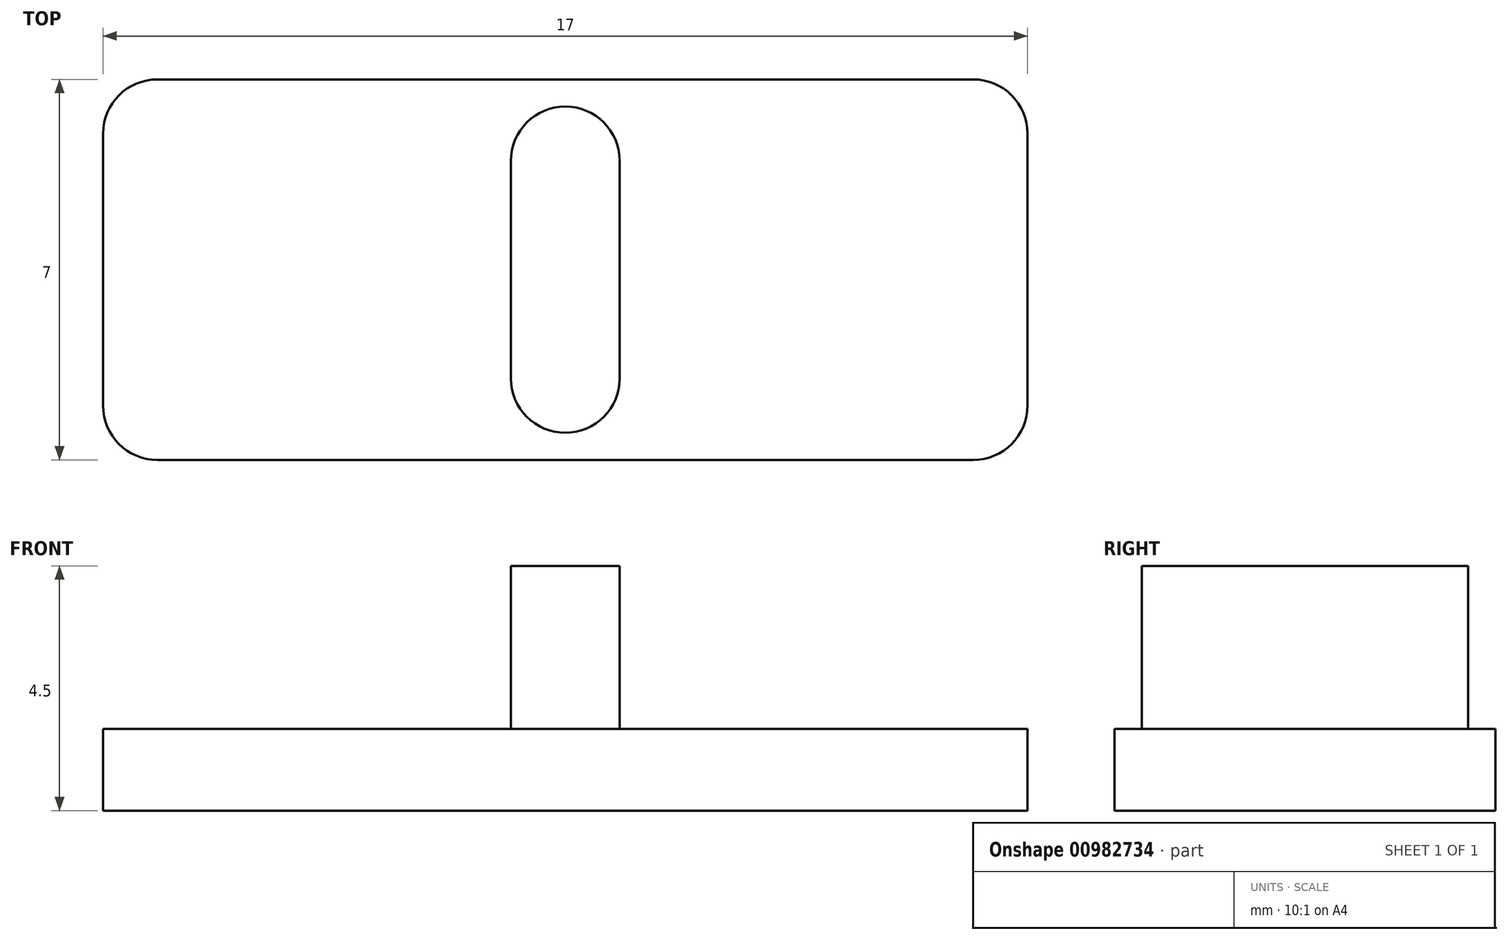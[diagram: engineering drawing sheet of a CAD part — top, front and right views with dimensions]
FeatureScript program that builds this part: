
annotation { "Feature Type Name" : "Feature", "Feature Type Description" : "" }
export const myFeature = defineFeature(function(context is Context, id is Id, definition is map)
    precondition{}
    {
        {
            var Q0;
            Q0=qCreatedBy(makeId("Top.planeOp"),FACE);
            var sketch = newSketch(context, id + "F0", { "sketchPlane" : qUnion([Q0])});
            skLineSegment(sketch, "E0.bottom", {"start": v(8.5, 3.5) * mm, "end": v(-8.5, 3.5) * mm});
            skLineSegment(sketch, "E0.top", {"start": v(8.5, -3.5) * mm, "end": v(-8.5, -3.5) * mm});
            skLineSegment(sketch, "E0.left", {"start": v(8.5, 3.5) * mm, "end": v(8.5, -3.5) * mm});
            skLineSegment(sketch, "E0.right", {"start": v(-8.5, 3.5) * mm, "end": v(-8.5, -3.5) * mm});
            skPoint(sketch, "E0.middle", {"position": v(0, 0) * mm});
            skSolve(sketch);
        }
        {
            var Q0;
            Q0=makeQuery(id+"F0.imprint","IMPRINT",FACE,{"disambiguationData":[TD([[makeQuery(id+"F0.imprint","IMPRINT",EDGE,{"derivedFrom":sQuery(id+"F0.wireOp",EDGE,"E0.bottom")}),1.0]])]});
            extrude(context, id + "F1", {"entities" : qUnion([Q0]), "depth" : 1.5 * mm, "offsetDistance" : 25 * mm});
        }
        {
            var Q0;
            Q0=makeQuery(id+"F1.opExtrude","CAP_FACE",FACE,{"disambiguationData":[OSD([sQuery(id+"F0.wireOp",EDGE,"E0.bottom"),sQuery(id+"F0.wireOp",EDGE,"E0.top"),sQuery(id+"F0.wireOp",EDGE,"E0.left"),sQuery(id+"F0.wireOp",EDGE,"E0.right")])],"isStart":false});
            var sketch = newSketch(context, id + "F2", { "sketchPlane" : qUnion([Q0])});
            skLineSegment(sketch, "E1.bottom", {"start": v(1, 2) * mm, "end": v(-1, 2) * mm});
            skLineSegment(sketch, "E1.top", {"start": v(1, -2) * mm, "end": v(-1, -2) * mm});
            skLineSegment(sketch, "E1.left", {"start": v(1, 2) * mm, "end": v(1, -2) * mm});
            skLineSegment(sketch, "E1.right", {"start": v(-1, 2) * mm, "end": v(-1, -2) * mm});
            skPoint(sketch, "E1.middle", {"position": v(0, 0) * mm});
            skArc(sketch, "E2", {"start": v(-1, 2) * mm, "mid": v(0, 3) * mm, "end": v(1, 2) * mm});
            skArc(sketch, "E3", {"start": v(-1, -2) * mm, "mid": v(0, -3) * mm, "end": v(1, -2) * mm});
            skSolve(sketch);
        }
        {
            var Q0;
            Q0=makeQuery(id+"F2.imprint","IMPRINT",FACE,{"disambiguationData":[TD([[makeQuery(id+"F2.imprint","IMPRINT",EDGE,{"derivedFrom":sQuery(id+"F2.wireOp",EDGE,"E1.top")}),1.0]])]});
            var Q1;
            Q1=makeQuery(id+"F2.imprint","IMPRINT",FACE,{"disambiguationData":[TD([[makeQuery(id+"F2.imprint","IMPRINT",EDGE,{"derivedFrom":sQuery(id+"F2.wireOp",EDGE,"E1.bottom")}),1.0]])]});
            var Q2;
            Q2=makeQuery(id+"F2.imprint","IMPRINT",FACE,{"disambiguationData":[TD([[makeQuery(id+"F2.imprint","IMPRINT",EDGE,{"derivedFrom":sQuery(id+"F2.wireOp",EDGE,"E1.bottom")}),-1.0]])]});
            extrude(context, id + "F3", {"entities" : qUnion([Q0, Q1, Q2]), "operationType" : NewBodyOperationType.ADD, "depth" : 3 * mm, "offsetDistance" : 25 * mm});
        }
        {
            var Q0;
            Q0=makeQuery(id+"F1.opExtrude","SWEPT_EDGE",EDGE,{"disambiguationData":[OSD([sQuery(id+"F0.wireOp",EDGE,"E0.bottom"),sQuery(id+"F0.wireOp",EDGE,"E0.right")])]});
            var Q1;
            Q1=makeQuery(id+"F1.opExtrude","SWEPT_EDGE",EDGE,{"disambiguationData":[OSD([sQuery(id+"F0.wireOp",EDGE,"E0.top"),sQuery(id+"F0.wireOp",EDGE,"E0.right")])]});
            var Q2;
            Q2=makeQuery(id+"F1.opExtrude","SWEPT_EDGE",EDGE,{"disambiguationData":[OSD([sQuery(id+"F0.wireOp",EDGE,"E0.bottom"),sQuery(id+"F0.wireOp",EDGE,"E0.left")])]});
            var Q3;
            Q3=makeQuery(id+"F1.opExtrude","SWEPT_EDGE",EDGE,{"disambiguationData":[OSD([sQuery(id+"F0.wireOp",EDGE,"E0.top"),sQuery(id+"F0.wireOp",EDGE,"E0.left")])]});
            fillet(context, id + "F4", {"entities" : qUnion([Q0, Q1, Q2, Q3]), "radius" : 1 * mm, "tangentPropagation" : true, "allowEdgeOverflow" : false});
        }
    });
